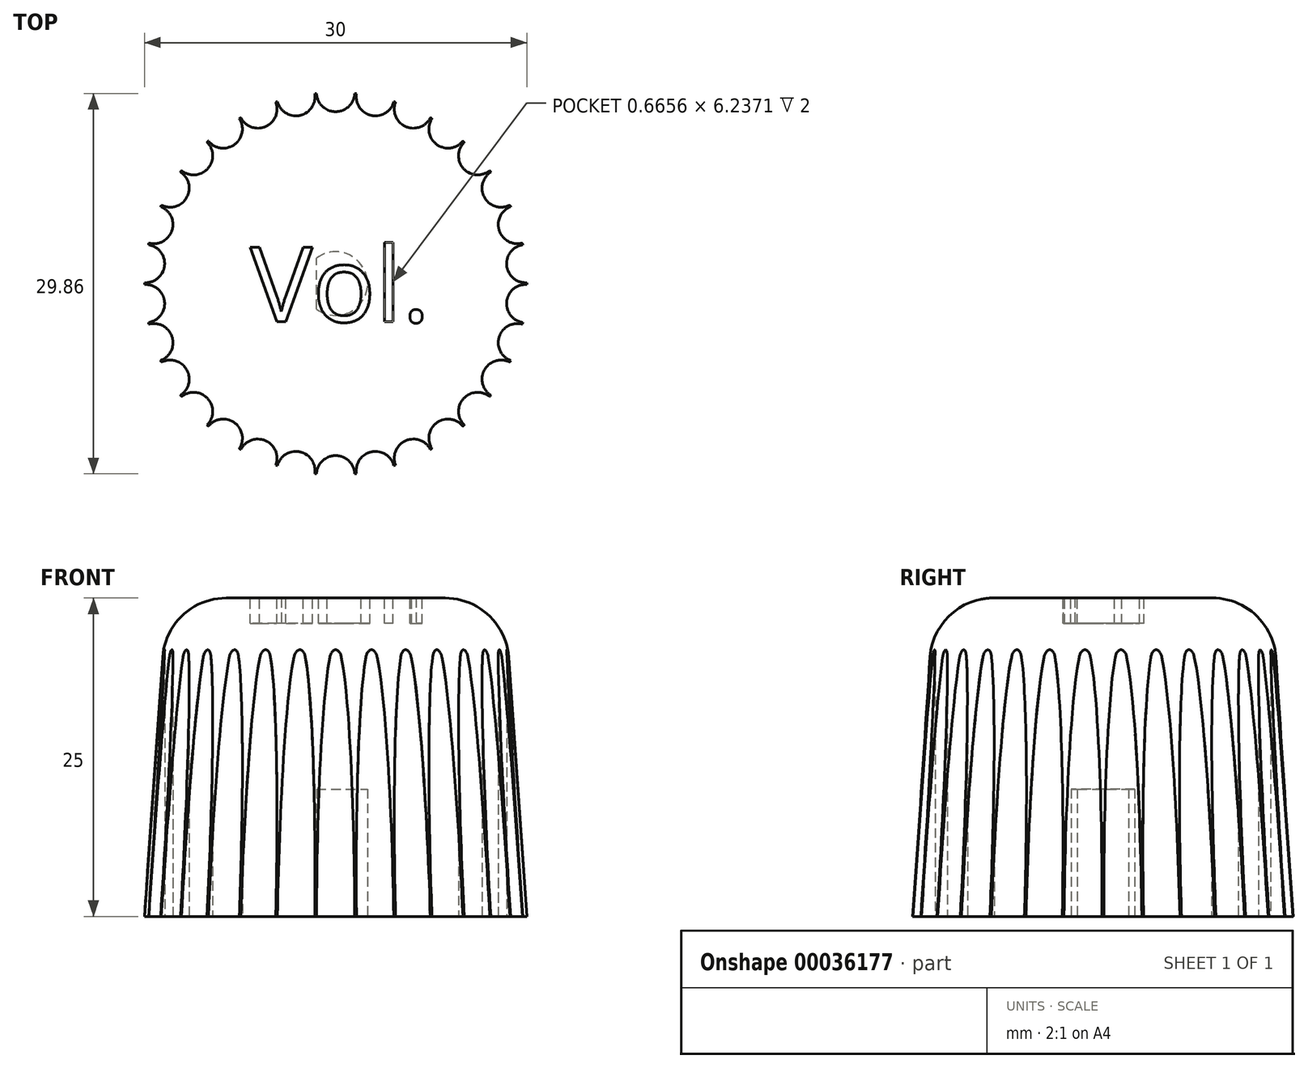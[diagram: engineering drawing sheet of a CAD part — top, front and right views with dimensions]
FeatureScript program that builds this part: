
annotation { "Feature Type Name" : "Feature", "Feature Type Description" : "" }
export const myFeature = defineFeature(function(context is Context, id is Id, definition is map)
    precondition{}
    {
        {
            var Q0;
            Q0=qCreatedBy(makeId("Top.planeOp"),FACE);
            var sketch = newSketch(context, id + "F0", { "sketchPlane" : qUnion([Q0])});
            skCircle(sketch, "E0", {"center": v(0, 0) * mm, "radius": 15 * mm});
            skSolve(sketch);
        }
        {
            var Q0;
            Q0=makeQuery(id+"F0.imprint","IMPRINT",FACE,{"disambiguationData":[TD([[makeQuery(id+"F0.imprint","IMPRINT",EDGE,{"derivedFrom":sQuery(id+"F0.wireOp",EDGE,"E0")}),1.0]])]});
            extrude(context, id + "F1", {"entities" : qUnion([Q0]), "depth" : 25 * mm, "hasDraft" : true, "draftAngle" : 4 * degree, "draftPullDirection" : true});
        }
        {
            var Q0;
            Q0=makeQuery(id+"F1.opExtrude","CAP_FACE",FACE,{"disambiguationData":[OSD([sQuery(id+"F0.wireOp",EDGE,"E0")])],"isStart":true});
            var sketch = newSketch(context, id + "F2", { "sketchPlane" : qUnion([Q0])});
            skCircle(sketch, "E1", {"center": v(0, -15) * mm, "radius": 1.5 * mm});
            skCircle(sketch, "E2.1.0", {"center": v(3.12, -14.67) * mm, "radius": 1.5 * mm});
            skCircle(sketch, "E2.2.0", {"center": v(6.1, -13.7) * mm, "radius": 1.5 * mm});
            skCircle(sketch, "E2.3.0", {"center": v(8.82, -12.14) * mm, "radius": 1.5 * mm});
            skCircle(sketch, "E2.4.0", {"center": v(11.15, -10.04) * mm, "radius": 1.5 * mm});
            skCircle(sketch, "E2.5.0", {"center": v(13, -7.5) * mm, "radius": 1.5 * mm});
            skCircle(sketch, "E2.6.0", {"center": v(14.27, -4.64) * mm, "radius": 1.5 * mm});
            skCircle(sketch, "E2.7.0", {"center": v(14.92, -1.57) * mm, "radius": 1.5 * mm});
            skCircle(sketch, "E2.8.0", {"center": v(14.92, 1.57) * mm, "radius": 1.5 * mm});
            skCircle(sketch, "E2.9.0", {"center": v(14.27, 4.64) * mm, "radius": 1.5 * mm});
            skPoint(sketch, "E2.center", {"position": v(0, 0) * mm});
            skCircle(sketch, "E3.1.10.0", {"center": v(13, 7.5) * mm, "radius": 1.5 * mm});
            skCircle(sketch, "E4.1.11.0", {"center": v(11.15, 10.04) * mm, "radius": 1.5 * mm});
            skCircle(sketch, "E5.1.12.0", {"center": v(8.82, 12.14) * mm, "radius": 1.5 * mm});
            skCircle(sketch, "E6.1.13.0", {"center": v(6.1, 13.7) * mm, "radius": 1.5 * mm});
            skCircle(sketch, "E7.1.14.0", {"center": v(3.12, 14.67) * mm, "radius": 1.5 * mm});
            skCircle(sketch, "E8.1.15.0", {"center": v(0, 15) * mm, "radius": 1.5 * mm});
            skCircle(sketch, "E8.1.16.0", {"center": v(-3.12, 14.67) * mm, "radius": 1.5 * mm});
            skCircle(sketch, "E8.1.17.0", {"center": v(-6.1, 13.7) * mm, "radius": 1.5 * mm});
            skCircle(sketch, "E9.1.18.0", {"center": v(-8.82, 12.14) * mm, "radius": 1.5 * mm});
            skCircle(sketch, "E9.1.19.0", {"center": v(-11.15, 10.04) * mm, "radius": 1.5 * mm});
            skCircle(sketch, "E9.1.20.0", {"center": v(-13, 7.5) * mm, "radius": 1.5 * mm});
            skCircle(sketch, "E10.1.21.0", {"center": v(-14.27, 4.64) * mm, "radius": 1.5 * mm});
            skCircle(sketch, "E10.1.22.0", {"center": v(-14.92, 1.57) * mm, "radius": 1.5 * mm});
            skCircle(sketch, "E11.1.23.0", {"center": v(-14.92, -1.57) * mm, "radius": 1.5 * mm});
            skCircle(sketch, "E12.1.24.0", {"center": v(-14.27, -4.64) * mm, "radius": 1.5 * mm});
            skCircle(sketch, "E12.1.25.0", {"center": v(-13, -7.5) * mm, "radius": 1.5 * mm});
            skCircle(sketch, "E12.1.26.0", {"center": v(-11.15, -10.04) * mm, "radius": 1.5 * mm});
            skCircle(sketch, "E12.1.27.0", {"center": v(-8.82, -12.14) * mm, "radius": 1.5 * mm});
            skCircle(sketch, "E12.1.28.0", {"center": v(-6.1, -13.7) * mm, "radius": 1.5 * mm});
            skCircle(sketch, "E13.1.29.0", {"center": v(-3.12, -14.67) * mm, "radius": 1.5 * mm});
            skSolve(sketch);
        }
        {
            var Q0;
            Q0 = qSketchRegion(id + "F2", true);
            extrude(context, id + "F3", {"entities" : qUnion([Q0]), "operationType" : NewBodyOperationType.REMOVE, "oppositeDirection" : true, "depth" : 25 * mm});
        }
        {
            var Q0;
            Q0=makeQuery(id+"F1.opExtrude","CAP_EDGE",EDGE,{"disambiguationData":[OSD([sQuery(id+"F0.wireOp",EDGE,"E0")])],"isStart":false});
            fillet(context, id + "F4", {"entities" : qUnion([Q0]), "radius" : 5 * mm, "tangentPropagation" : true, "allowEdgeOverflow" : false});
        }
        {
            var Q0;
            Q0=makeQuery(id+"F1.opExtrude","CAP_FACE",FACE,{"disambiguationData":[OSD([sQuery(id+"F0.wireOp",EDGE,"E0")])],"isStart":true});
            var sketch = newSketch(context, id + "F5", { "sketchPlane" : qUnion([Q0])});
            skArc(sketch, "E14", {"start": v(-1.5, -2) * mm, "mid": v(2.5, 0) * mm, "end": v(-1.5, 2) * mm});
            skLineSegment(sketch, "E15", {"start": v(-1.5, 2) * mm, "end": v(-1.5, -2) * mm});
            skSolve(sketch);
        }
        {
            var Q0;
            Q0 = qSketchRegion(id + "F5", true);
            extrude(context, id + "F6", {"entities" : qUnion([Q0]), "operationType" : NewBodyOperationType.REMOVE, "oppositeDirection" : true, "depth" : 10 * mm});
        }
        {
            var Q0;
            Q0=makeQuery(id+"F1.opExtrude","CAP_FACE",FACE,{"disambiguationData":[OSD([sQuery(id+"F0.wireOp",EDGE,"E0")])],"isStart":false});
            var sketch = newSketch(context, id + "F7", { "sketchPlane" : qUnion([Q0])});
            skText(sketch, "E16", { "text": "Vol.", "fontName": "OpenSans-Regular.ttf"});
            skPoint(sketch, "E17.startSnap0", {"position": v(0, 4.23) * mm});
            skLineSegment(sketch, "E18", {"start": v(0, 8.59) * mm, "end": v(0, -8.59) * mm, "construction": true});
            const initialGuessF7  = {"E16": [-0.0067, -0.003, 1, 0, 0.00591]};
            skSetInitialGuess(sketch, initialGuessF7);
            skSolve(sketch);
        }
        {
            var Q0;
            Q0 = qSketchRegion(id + "F7", true);
            extrude(context, id + "F8", {"entities" : qUnion([Q0]), "operationType" : NewBodyOperationType.REMOVE, "oppositeDirection" : true, "depth" : 2 * mm});
        }
    });
